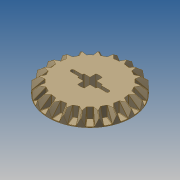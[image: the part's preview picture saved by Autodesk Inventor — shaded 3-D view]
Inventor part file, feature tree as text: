
AUTODESK INVENTOR PART (.ipt)
format: ipt  version: 2022.2 (Build 262287000, 287)  size: 4,621,824 bytes
history: native  units: in
note: dims shown in document units (in); Inventor stores cm internally (conversion verified against a paired STEP export)
features: sketch x7, revolve x3, extrude x3, projected_geometry x3, fillet x2, plane x2, other x1, loft x1, pattern_circular x1
ambient origin geometry x8: Origin, YZ Plane, XZ Plane, XY Plane, X Axis, Y Axis, Z Axis, Center Point
bodies: Solid1 (feature_tree)
feature tree (23):
  sketch  "Sketch2"  dims[d7=90.0deg d8=0.189in]
  revolve  "Revolution1"  [1 undecoded]
  sketch  "Sketch4"  dims[d14=0.6278in d17=0.0498in]
  sketch  "Sketch6"  dims[d30=90.0deg d32=0.0709in d47=0.0039in d48=7.874in d49=360.0deg]
  revolve  "Revolution3"  [1 undecoded]
  other  "Work Axis3"
  loft  "Loft4"
  revolve  "Revolution2"  [1 undecoded]
  fillet  "Fillet1"  Radius=0.0039in
  pattern_circular  "Circular Pattern1"  Count=20 Angle=360.0deg
  extrude  "Extrusion1"  Depth=0.0039in
  sketch  "Sketch14"  dims[d55=0.0236in d56=0.0079in d57=0.8189in d58=0.6299in d59=0.0472in d60=0.5354in d61=0.7244in d62=0.0626in d63=0.0in d64=90.0deg d65=0.0in d66=90.0deg d67=0.0in d68=90.0deg d69=0.378in d70=0.0315in d71=0.378in d72=0.0937in d73=0.4724in d74=0.2835in d75=0.0472in d76=0.0in d77=0.0945in d78=0.0in]
  extrude  "Extrusion2"  Depth=0.1102in
  extrude  "Extrusion3"  Depth=0.0472in
  fillet  "Fillet2"  Radius=0.8189in
  sketch  "Sketch3"  dims[d10=0.063in d12=0.3937in d13=0.0in]
  plane  "Work Plane11"
  sketch  "Sketch12"  dims[d51=0.0024in d52=0.0039in]
  sketch  "Sketch13"  dims[d53=0.1102in d54=0.1102in]
  plane  "Work Plane13"
  projected_geometry  "Project Cut Edges2"
  projected_geometry  "Project Cut Edges3"
  projected_geometry  "Project Cut Edges4"
note: 3 required parameter values undecoded (feature->parameter linkage not recoverable at this tier; creation-order binding heuristic only, values carry confidence <= 0.55)
